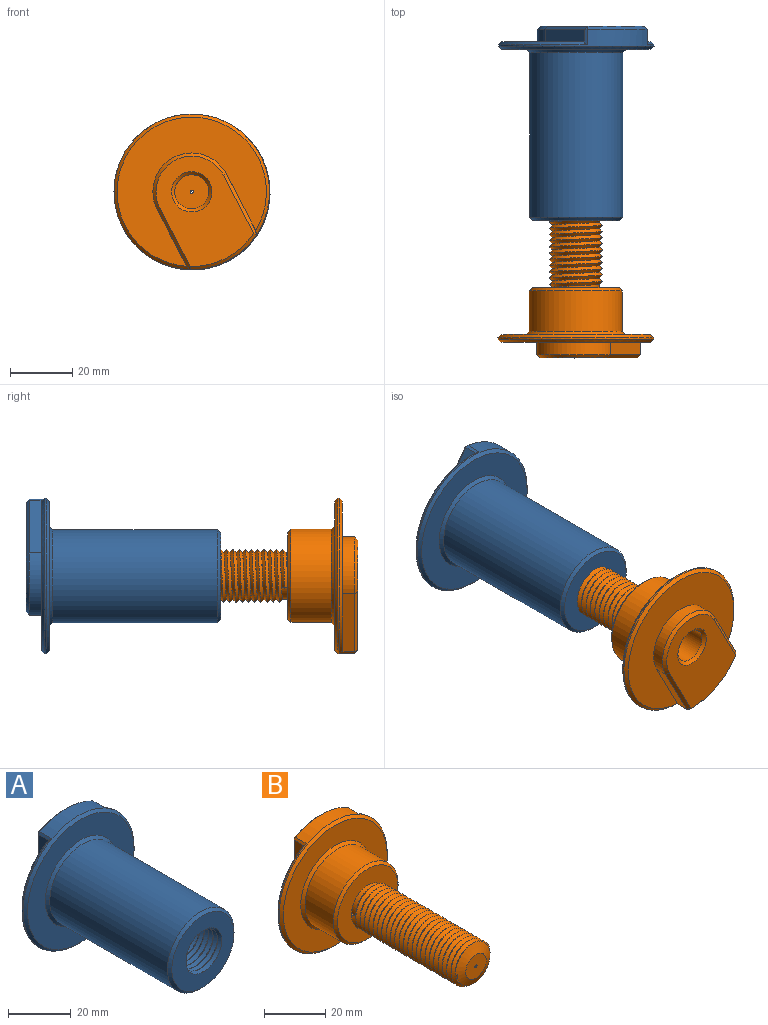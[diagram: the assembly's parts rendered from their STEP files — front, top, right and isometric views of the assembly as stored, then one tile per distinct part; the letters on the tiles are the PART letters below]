
ASSEMBLY  parts=2 mates=1
PART A: 30 faces, bbox 50.8x64.7x50.8 mm
  f0: cylinder r=7.6mm len=50mm, axis (0,-1,0), area 458.8mm2, adj f9,f10,f14,f15,f16
  f1: plane 21.07x4.5mm, normal (-1,0,0), area 84.4mm2, adj f2,f7,f20,f21,f23
  f2: cylinder r=12.5mm len=25mm, axis (0,1,0), area 157.1mm2, adj f1,f3,f7,f26
  f3: plane 21.07x4.5mm, normal (1,0,0), area 84.4mm2, adj f2,f7,f21,f24,f28
  f4: plane 35.5x23mm, normal (0,1,0), area 622.8mm2, adj f19,f23,f25,f26,f28
  f5: cylinder r=25mm len=50mm, axis (0,1,0), area 203.5mm2, adj f20,f21,f24,f25,f29
  f6: plane 48x48mm, normal (0,-1,0), area 1005.3mm2, adj f18,f29
  f7: plane 48x44.49mm, normal (0,1,0), area 992.5mm2, adj f1,f2,f3,f21
  f8: cylinder r=15mm len=53mm, axis (0,1,0), area 4995.1mm2, adj f17,f18
  f9: plane 28.84x28.84mm, normal (0,-1,0), area 409.9mm2, adj f0,f15,f16,f17
  f10: plane 15.2x15.2mm, normal (0,-1,0), area 180.7mm2, adj f0,f13
  f11: cylinder r=5.05mm len=10.1mm, axis (0,1,0), area 317.3mm2, adj f12,f19
  f12: plane 10.1x10.1mm, normal (0,1,0), area 79.3mm2, adj f11,f13
  f13: cylinder r=0.5mm len=1.5mm, axis (0,1,0), area 4.7mm2, adj f10,f12
  f14: plane 1.98x0.99mm, normal (0,0,-1), area 1mm2, adj f0,f15,f16
  f15: bspline ~50.99x19.84mm, area 1758.2mm2, adj f0,f9,f14,f16
  f16: bspline ~50.32x19.84mm, area 1729.4mm2, adj f0,f9,f14,f15
  f17: cone r=14mm half-angle=45deg, axis (0,1,0), area 128.8mm2, adj f8,f9
  f18: cone r=15mm half-angle=45deg, axis (0,1,0), area 137.7mm2, adj f6,f8
  f19: cone r=5.05mm half-angle=45deg, axis (0,1,0), area 49.3mm2, adj f4,f11
  f20: plane 5.01x0.89mm, normal (-0.86,0,0.51), area 4.8mm2, adj f1,f5,f21,f22
  f21: cone r=25mm half-angle=45deg, axis (0,-1,0), area 181mm2, adj f1,f3,f5,f7,f20,f24
  f22: plane 1x1mm, normal (-0.65,0.65,0.39), area 0.7mm2, adj f20,f23,f25
  f23: plane 21.07x1mm, normal (-0.71,0.71,0), area 29.8mm2, adj f1,f4,f22,f26
  f24: plane 5.01x0.89mm, normal (0.86,0,0.51), area 4.8mm2, adj f3,f5,f21,f27
  f25: cone r=25mm half-angle=45deg, axis (0,-1,0), area 34.6mm2, adj f4,f5,f22,f27
  f26: cone r=12.5mm half-angle=45deg, axis (0,-1,0), area 53.3mm2, adj f2,f4,f23,f28
  f27: plane 1x1mm, normal (0.65,0.65,0.39), area 0.7mm2, adj f24,f25,f28
  f28: plane 21.07x1mm, normal (0.71,0.71,0), area 29.8mm2, adj f3,f4,f26,f27
  f29: cone r=24mm half-angle=45deg, axis (0,1,0), area 217.7mm2, adj f5,f6
PART B: 56 faces, bbox 50x72.5x50 mm
  f0: plane 9.48x9.48mm, normal (0,-1,0), area 69.8mm2, adj f53,f55
  f1: cylinder r=7.5mm len=15mm, axis (0,1,0), area 48.1mm2, adj f2,f34,f36,f38
  f2: cylinder r=7.5mm len=15mm, axis (0,1,0), area 1mm2, adj f1,f3,f37,f38
  f3: cylinder r=7.5mm len=15mm, axis (0,1,0), area 0.9mm2, adj f2,f4,f37,f38
  f4: cylinder r=7.5mm len=15mm, axis (0,1,0), area 0.9mm2, adj f3,f5,f37,f38
  f5: cylinder r=7.5mm len=15mm, axis (0,1,0), area 0.9mm2, adj f4,f6,f37,f38
  f6: cylinder r=7.5mm len=15mm, axis (0,1,0), area 0.9mm2, adj f5,f7,f37,f38
  f7: cylinder r=7.5mm len=15mm, axis (0,1,0), area 1mm2, adj f6,f8,f37,f38
  f8: cylinder r=7.5mm len=15mm, axis (0,1,0), area 1mm2, adj f7,f9,f37,f38
  f9: cylinder r=7.5mm len=15mm, axis (0,1,0), area 0.9mm2, adj f8,f10,f37,f38
  f10: cylinder r=7.5mm len=15mm, axis (0,1,0), area 0.9mm2, adj f9,f11,f37,f38
  f11: cylinder r=7.5mm len=15mm, axis (0,1,0), area 1mm2, adj f10,f12,f37,f38
  f12: cylinder r=7.5mm len=15mm, axis (0,1,0), area 0.9mm2, adj f11,f13,f37,f38
  f13: cylinder r=7.5mm len=15mm, axis (0,1,0), area 0.9mm2, adj f12,f14,f37,f38
  f14: cylinder r=7.5mm len=15mm, axis (0,1,0), area 0.9mm2, adj f13,f15,f37,f38
  f15: cylinder r=7.5mm len=15mm, axis (0,1,0), area 0.9mm2, adj f14,f16,f37,f38
  f16: cylinder r=7.5mm len=15mm, axis (0,1,0), area 1mm2, adj f15,f17,f37,f38
  f17: cylinder r=7.5mm len=15mm, axis (0,1,0), area 1mm2, adj f16,f18,f37,f38
  f18: cylinder r=7.5mm len=15mm, axis (0,1,0), area 0.9mm2, adj f17,f19,f37,f38
  f19: cylinder r=7.5mm len=15mm, axis (0,1,0), area 0.9mm2, adj f18,f20,f37,f38
  f20: cylinder r=7.5mm len=15mm, axis (0,1,0), area 1mm2, adj f19,f21,f37,f38
  f21: cylinder r=7.5mm len=15mm, axis (0,1,0), area 0.9mm2, adj f20,f22,f37,f38
  f22: cylinder r=7.5mm len=15mm, axis (0,1,0), area 0.9mm2, adj f21,f23,f37,f38
  f23: cylinder r=7.5mm len=15mm, axis (0,1,0), area 0.9mm2, adj f22,f24,f37,f38
  f24: cylinder r=7.5mm len=15mm, axis (0,1,0), area 0.9mm2, adj f23,f25,f37,f38
  f25: cylinder r=7.5mm len=14.58mm, axis (0,1,0), area 9.5mm2, adj f24,f35,f37,f55
  f26: plane 21.07x4.5mm, normal (-1,0,0), area 84.4mm2, adj f27,f32,f42,f47,f49
  f27: cylinder r=12.5mm len=25mm, axis (0,1,0), area 157.1mm2, adj f26,f28,f32,f41
  f28: plane 21.07x4.5mm, normal (1,0,0), area 84.4mm2, adj f27,f32,f44,f48,f49
  f29: plane 35.5x23mm, normal (0,1,0), area 605.7mm2, adj f41,f42,f43,f44,f54
  f30: cylinder r=25mm len=50mm, axis (0,1,0), area 203.5mm2, adj f43,f47,f48,f49,f50
  f31: plane 48x48mm, normal (0,-1,0), area 1005.3mm2, adj f39,f50
  f32: plane 48x44.49mm, normal (0,1,0), area 992.5mm2, adj f26,f27,f28,f49
  f33: cylinder r=15mm len=30mm, axis (0,1,0), area 1225.2mm2, adj f39,f40
  f34: plane 28x28mm, normal (0,-1,0), area 439mm2, adj f1,f40
  f35: plane 0.88x0.63mm, normal (0,0,-1), area 0.3mm2, adj f25,f38,f55
  f36: plane 1.98x0.99mm, normal (0,0,1), area 1mm2, adj f1,f37,f38
  f37: bspline ~48.66x19.61mm, area 1660.4mm2, adj f2,f3,f4,f5,f6,f7,f8,f9
  f38: bspline ~48.99x19.61mm, area 1686mm2, adj f1,f2,f3,f4,f5,f6,f7,f8
  f39: cone r=15mm half-angle=45deg, axis (0,1,0), area 137.7mm2, adj f31,f33
  f40: cone r=14mm half-angle=45deg, axis (0,1,0), area 128.8mm2, adj f33,f34
  f41: cone r=12.5mm half-angle=45deg, axis (0,-1,0), area 53.3mm2, adj f27,f29,f42,f44
  f42: plane 21.07x1mm, normal (-0.71,0.71,0), area 29.8mm2, adj f26,f29,f41,f45
  f43: cone r=25mm half-angle=45deg, axis (0,-1,0), area 34.6mm2, adj f29,f30,f45,f46
  f44: plane 21.07x1mm, normal (0.71,0.71,0), area 29.8mm2, adj f28,f29,f41,f46
  f45: plane 1x1mm, normal (-0.65,0.65,0.39), area 0.7mm2, adj f42,f43,f47
  f46: plane 1x1mm, normal (0.65,0.65,0.39), area 0.7mm2, adj f43,f44,f48
  f47: plane 5.01x0.89mm, normal (-0.86,0,0.51), area 4.8mm2, adj f26,f30,f45,f49
  f48: plane 5.01x0.89mm, normal (0.86,0,0.51), area 4.8mm2, adj f28,f30,f46,f49
  f49: cone r=25mm half-angle=45deg, axis (0,-1,0), area 181mm2, adj f26,f28,f30,f32,f47,f48
  f50: cone r=24mm half-angle=45deg, axis (0,1,0), area 217.7mm2, adj f30,f31
  f51: cylinder r=5.49mm len=11.5mm, axis (0,1,0), area 396.4mm2, adj f52,f54
  f52: plane 10.97x10.97mm, normal (0,1,0), area 93.8mm2, adj f51,f53
  f53: cylinder r=0.5mm len=60mm, axis (0,1,0), area 188.5mm2, adj f0,f52
  f54: cone r=5.49mm half-angle=45deg, axis (0,1,0), area 53.2mm2, adj f29,f51
  f55: cone r=8.49mm half-angle=68.2deg, axis (0,1,0), area 133.2mm2, adj f0,f25,f35,f37,f38
PLACE A rot(axis=(0,1,0),36.9deg) t=(-28.72,2.21,14.16)mm
PLACE B rot(axis=(0.97,0,0.24),180deg) t=(-28.88,-104.43,14.27)mm
MATE cylindrical A.f9 <-> B.f33  axis (0,-1,0) through (-28.88,-60.29,14.27)mm
